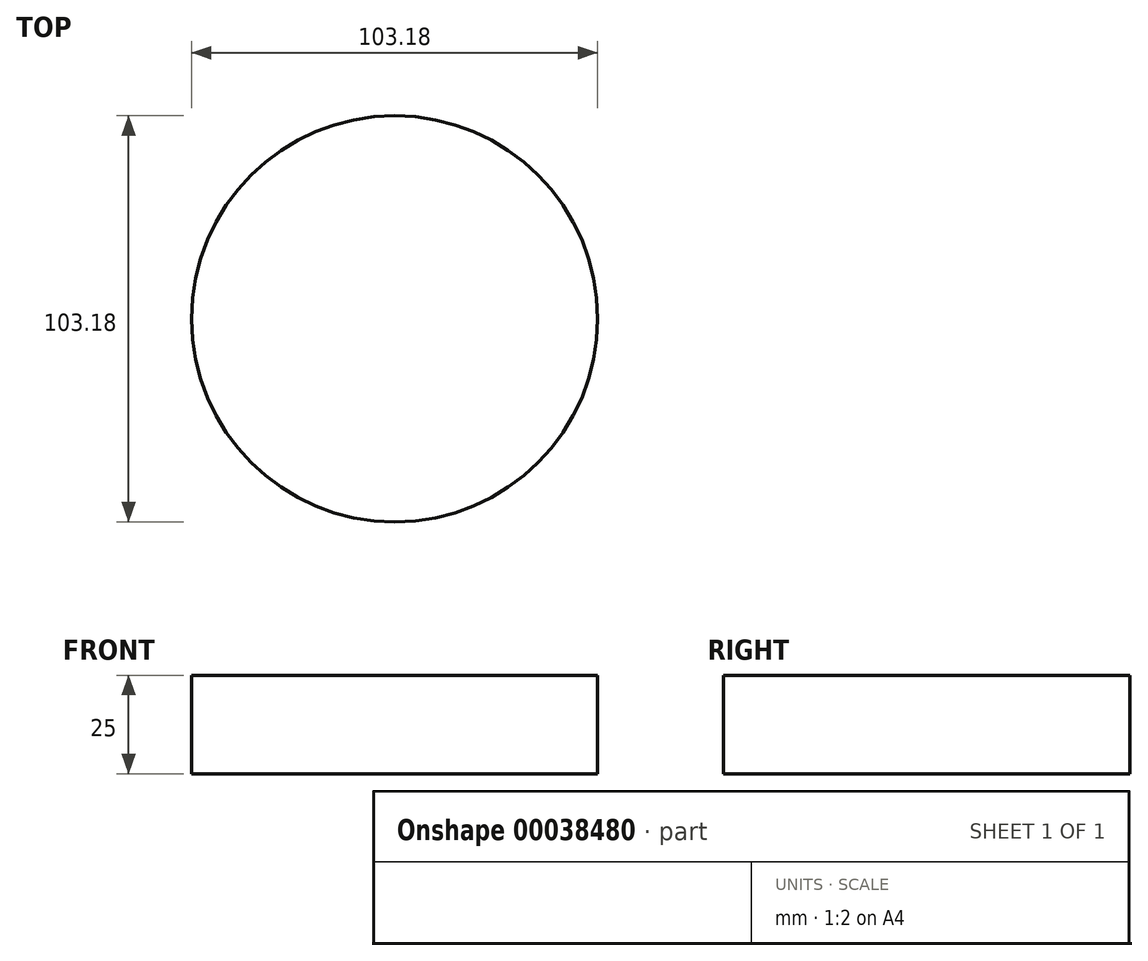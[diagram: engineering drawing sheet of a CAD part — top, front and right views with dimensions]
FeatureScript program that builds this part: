
annotation { "Feature Type Name" : "Feature", "Feature Type Description" : "" }
export const myFeature = defineFeature(function(context is Context, id is Id, definition is map)
    precondition{}
    {
        {
            var Q0;
            Q0=qCreatedBy(makeId("Top.planeOp"),FACE);
            var sketch = newSketch(context, id + "F0", { "sketchPlane" : qUnion([Q0])});
            skCircle(sketch, "E0", {"center": v(0, 0) * mm, "radius": 51.59 * mm});
            skSolve(sketch);
        }
        {
            var Q0;
            Q0=makeQuery(id+"F0.imprint","IMPRINT",FACE,{"disambiguationData":[TD([[makeQuery(id+"F0.imprint","IMPRINT",EDGE,{"derivedFrom":sQuery(id+"F0.wireOp",EDGE,"E0")}),1.0]])]});
            extrude(context, id + "F1", {"entities" : qUnion([Q0]), "depth" : 25 * mm});
        }
    });
